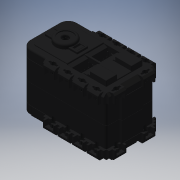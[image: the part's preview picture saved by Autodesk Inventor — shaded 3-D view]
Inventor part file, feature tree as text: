
AUTODESK INVENTOR PART (.ipt)
format: ipt  version: 2016 (Build 200138000, 138)  size: 2,573,824 bytes
history: native  units: in
note: dims shown in document units (in); Inventor stores cm internally (conversion verified against a paired STEP export)
features: imported_body x1, sketch x1, extrude x1, hole x1
ambient origin geometry x8: Origin, YZ Plane, XZ Plane, XY Plane, X Axis, Y Axis, Z Axis, Center Point
bodies: Solid1 (feature_tree), Solid2 (feature_tree)
feature tree (4):
  imported_body  "Base1"
  sketch  "Sketch2"  dims[d0=0.8661in d1=0.0787in d2=0.0787in d3=0.0787in d4=0.0787in d5=0.0787in d6=0.0in d7=0.0906in d8=0.2362in d9=0.1575in d10=0.0787in d11=90.0deg d12=0.315in d13=0.8108in]
  extrude  "Extrusion1"  Depth=0.0787in
  hole  "Hole1"  [1 undecoded]
note: 1 required parameter value undecoded (feature->parameter linkage not recoverable at this tier; creation-order binding heuristic only, values carry confidence <= 0.55)
